# Revit family: FireFighting_Firemain-Booster-Suction-Set_Galvin_150TE
name_source: partatom
category: Mechanical Equipment
revit_build: Autodesk Revit MEP 2012 (Build: 20110916_2132(x64)
units: mm (PartAtom-declared; Revit-internal decimal feet)

## types (1)
- 380142SR
    Assembly Code = D4030
    Description = WA Firemain Booster & Suction Riser Set 150TE with Cabinet (Painted)
    DimDepth = 600 mm
    DimHeight = 1300 mm  [stored 4.26509 ft]
    DimInletRadius = 50 mm  [stored 0.164042 ft]
    DimWidth = 1165 mm  [stored 3.82218 ft]
    FilterObject_ANZRS = 380142SR
    FlowRate = 0.00 L/s
    Instructions = http://www.galvinengineering.com.au
    Keynote = 10520
    Manufacturer = Galvin Engineering
    Model = 380142SR
    ModifiedIssue_ANZRS = 20140330 $
    StyleOrType_ANZRS = Fire Fighting Equipment
    Type Comments = 380142SR
    URL = www.galvinengineering.com.au

note: [stored X ft] marks values corroborated as IEEE doubles in the binary element streams (Revit-internal decimal feet)

## geometry (parser evidence)
native form markers: Blend x4, Sweep x1
no freeform markers — native parametric forms only
